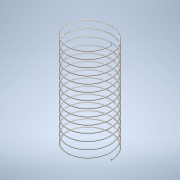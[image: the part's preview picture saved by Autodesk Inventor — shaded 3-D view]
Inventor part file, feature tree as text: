
AUTODESK INVENTOR PART (.ipt)
format: ipt  version: 2020 (Build 240168000, 168)  size: 350,720 bytes
history: native  units: mm
features: helix x1, other x1, sketch x1
ambient origin geometry x8: Origin, YZ Plane, XZ Plane, XY Plane, X Axis, Y Axis, Z Axis, Center Point
bodies: Solid1 (feature_tree)
feature tree (3):
  helix  "Coil1"  [1 undecoded]
  other  "Work Axis1"
  sketch  "Sketch1"  dims[d1=0.3mm d2=10.0mm d3=32.0mm d4=140.0mm d5=0.0mm d6=90.0deg d7=90.0deg d8=0.0mm d9=0.0mm]
note: 1 required parameter value undecoded (feature->parameter linkage not recoverable at this tier; creation-order binding heuristic only, values carry confidence <= 0.55)
